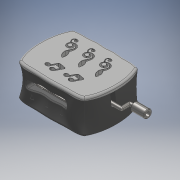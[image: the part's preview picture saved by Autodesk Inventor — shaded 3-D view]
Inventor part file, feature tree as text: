
AUTODESK INVENTOR PART (.ipt)
format: ipt  version: 2017 (Build 210142000, 142)  size: 9,125,376 bytes
history: native  units: mm
features: other x34, sketch x16, extrude x10, projected_geometry x6, chamfer x4, fillet x3, hole x2, pattern_linear x2, loft x1, imported_body x1
ambient origin geometry x8: Origin, YZ Plane, XZ Plane, XY Plane, X Axis, Y Axis, Z Axis, Center Point
bodies: Solide2 (feature_tree)
feature tree (79):
  other  "Kikkerland Music Box.iam"
  other  "Bedplate.ipt:1"
  other  "Right Feeder Tray Support.ipt:1"
  other  "Comb.ipt:1"
  other  "Screws.iam:1::Keyboard-91735A102.ipt:1"
  other  "Screws.iam:1::Gear Housing 91735A101.ipt:1"
  other  "Screws.iam:1::Gear Housing 91735A101.ipt:2"
  other  "Screws.iam:1::Tray Support 91737A069.ipt:1"
  other  "Screws.iam:1::Tray Support 91737A069.ipt:2"
  other  "Left Feeder Tray Support.ipt:1"
  other  "Drive Gear Housing.ipt:1"
  other  "Paper Feed Roller.ipt:1"
  other  "Feed Gear.ipt:1"
  other  "Branch Gear 1.ipt:1"
  other  "Crank Gear.ipt:1"
  other  "Washers.ipt:1"
  other  "Drum Plucker.ipt:1"
  other  "Plucker Gear Sm.ipt:1"
  other  "Plucker Gear Lg.ipt:1"
  other  "Branch Gear 2.ipt:1"
  other  "Lower Feeder Tray.ipt:1"
  other  "Upper Feeder Tray.ipt:1"
  other  "Hand Crank.ipt:1"
  other  "Wire Form.ipt:1"
  other  "Boite a musique"
  other  "Fond_boite"
  other  "Dessous"
  sketch  "Esquisse2"
  other  "Milieu"
  sketch  "Esquisse4"
  other  "Dessus"
  loft  "Lissage1"
  fillet  "Congé1"  Radius=35.0mm
  other  "Plan de construction5"
  other  "Scission1"
  extrude  "Ouverture_interieur"  Depth=25.0mm
  extrude  "Passage bras"  Depth=70.0mm
  extrude  "Entrée bande"  [1 undecoded]
  extrude  "Extrusion6"  Depth=25.0mm
  fillet  "Congé3"  Radius=75.0mm
  chamfer  "Chanfrein2"  Distance=9.375mm
  extrude  "Extrusion7"  Depth=9.375mm
  hole  "Perçage1"  [1 undecoded]
  fillet  "Congé4"  Radius=9.375mm
  extrude  "Extrusion9"  Depth=9.375mm
  extrude  "Extrusion10"  Depth=9.375mm
  hole  "Perçage2"  [1 undecoded]
  chamfer  "Chanfrein3"  Distance=12.5mm
  extrude  "Extrusion11"  Depth=12.5mm
  extrude  "Extrusion12"  Depth=12.5mm
  extrude  "Extrusion13"  Depth=12.5mm
  chamfer  "Chanfrein4"  Distance=12.5mm
  pattern_linear  "Réseau rectangulaire2"  Spacing1=12.5mm  [1 undecoded]
  pattern_linear  "Réseau rectangulaire3"  Spacing1=-18.0mm  [1 undecoded]
  chamfer  "Chanfrein5"  Distance=10.0mm
  other  "Plan de construction6"
  other  "Gravure1"
  sketch  "Esquisse5"
  sketch  "Esquisse8"
  sketch  "Esquisse9"
  sketch  "Esquisse10"
  sketch  "Esquisse12"
  sketch  "Esquisse13"
  projected_geometry  "Boucle projetée1"
  sketch  "Esquisse14"
  sketch  "Esquisse16"
  sketch  "Esquisse17"
  sketch  "Esquisse18"
  projected_geometry  "Boucle projetée2"
  projected_geometry  "Boucle projetée3"
  projected_geometry  "Boucle projetée4"
  sketch  "Esquisse19"
  sketch  "Esquisse20"
  projected_geometry  "Boucle projetée5"
  projected_geometry  "Boucle projetée6"
  sketch  "Esquisse21"
  sketch  "Esquisse22"
  other  "Couvercle"
  imported_body  "Base"
note: 5 required parameter values undecoded (feature->parameter linkage not recoverable at this tier; creation-order binding heuristic only, values carry confidence <= 0.55)
